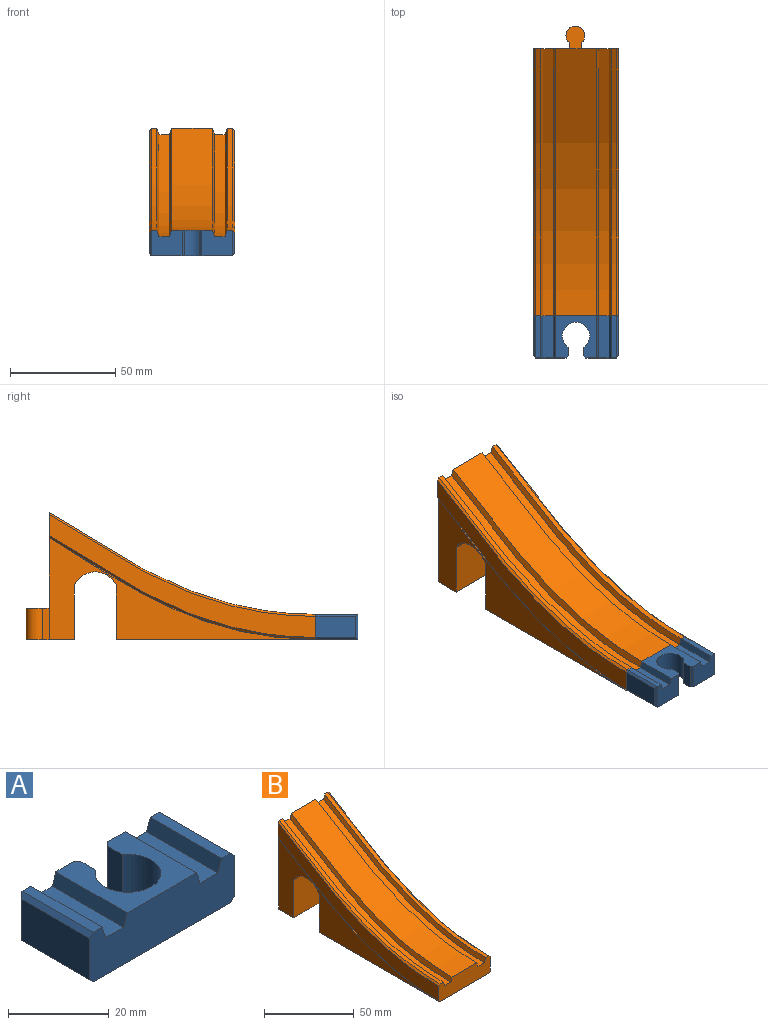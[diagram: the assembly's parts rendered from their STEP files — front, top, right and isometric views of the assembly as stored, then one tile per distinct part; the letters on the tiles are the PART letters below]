
ASSEMBLY  parts=2 mates=1
PART A: 26 faces, bbox 40.5x20x12 mm
  f0: plane 38.5x20mm, normal (0,0,-1), area 603.4mm2, adj f2,f13,f14,f15,f16,f17,f18,f21
  f1: plane 20x19.5mm, normal (0,0,1), area 223.4mm2, adj f2,f7,f8,f13,f14,f15,f16,f17
  f2: plane 14.51x12mm, normal (0,1,0), area 156.1mm2, adj f0,f1,f8,f9,f10,f11,f20,f21
  f3: plane 19x10mm, normal (1,0,0), area 190mm2, adj f14,f23,f24,f25
  f4: plane 20x2.5mm, normal (0,0,1), area 50mm2, adj f5,f13,f14,f24
  f5: plane 20x3mm, normal (-0.95,0,0.32), area 63.2mm2, adj f4,f6,f13,f14
  f6: plane 20x5mm, normal (0,0,1), area 100mm2, adj f5,f7,f13,f14
  f7: plane 20x3mm, normal (0.95,0,0.32), area 63.2mm2, adj f1,f6,f13,f14
  f8: plane 20x3mm, normal (-0.95,0,0.32), area 63.2mm2, adj f1,f2,f9,f14
  f9: plane 20x5mm, normal (0,0,1), area 100mm2, adj f2,f8,f10,f14
  f10: plane 20x3mm, normal (0.95,0,0.32), area 63.2mm2, adj f2,f9,f11,f14
  f11: plane 20x2.5mm, normal (0,0,1), area 50mm2, adj f2,f10,f14,f19
  f12: plane 19x10mm, normal (-1,0,0), area 190mm2, adj f14,f18,f19,f20
  f13: plane 14.49x12mm, normal (0,1,0), area 155.9mm2, adj f0,f1,f4,f5,f6,f7,f22,f25
  f14: plane 40.5x12mm, normal (0,-1,0), area 448mm2, adj f0,f1,f3,f4,f5,f6,f7,f8
  f15: cylinder r=6.5mm len=13mm, axis (0,0,1), area 394.2mm2, adj f0,f1,f16,f17
  f16: plane 12x4.19mm, normal (1,0,0), area 50.3mm2, adj f0,f1,f15,f21
  f17: plane 12x4.19mm, normal (-1,0,0), area 50.3mm2, adj f0,f1,f15,f22
  f18: plane 20x1mm, normal (-0.71,0,-0.71), area 27.6mm2, adj f0,f12,f14,f20
  f19: plane 20x1mm, normal (-0.71,0,0.71), area 27.6mm2, adj f11,f12,f14,f20
  f20: plane 12x1mm, normal (-0.71,0.71,0), area 15.6mm2, adj f2,f12,f18,f19
  f21: plane 12x1mm, normal (0.71,0.71,0), area 17mm2, adj f0,f1,f2,f16
  f22: plane 12x1mm, normal (-0.71,0.71,0), area 17mm2, adj f0,f1,f13,f17
  f23: plane 20x1mm, normal (0.71,0,-0.71), area 27.6mm2, adj f0,f3,f14,f25
  f24: plane 20x1mm, normal (0.71,0,0.71), area 27.6mm2, adj f3,f4,f14,f25
  f25: plane 12x1mm, normal (0.71,0.71,0), area 15.6mm2, adj f3,f13,f23,f24
PART B: 29 faces, bbox 40.5x235x97 mm
  f0: plane 60.46x40.5mm, normal (0,1,0), area 2251.5mm2, adj f1,f7,f8,f9,f10,f11,f12,f13
  f1: plane 39x22.96mm, normal (0,0,-1), area 544.8mm2, adj f0,f2,f23,f24,f25,f26,f27
  f2: plane 39x26mm, normal (0,-1,0), area 1014mm2, adj f1,f3,f23,f24
  f3: cylinder r=11.18mm len=39mm, axis (1,0,0), area 965.2mm2, adj f2,f4,f23,f24
  f4: plane 39x26mm, normal (0,1,0), area 1014mm2, adj f3,f6,f23,f24
  f5: plane 40.5x12mm, normal (0,-1,0), area 448mm2, adj f6,f8,f9,f10,f11,f12,f13,f14
  f6: plane 95x39mm, normal (0,0,-1), area 3705mm2, adj f4,f5,f7,f23,f24
  f7: extruded ~127x48.46mm, area 69.1mm2, adj f0,f6,f8,f24
  f8: bspline ~235x86mm, area 187.7mm2, adj f0,f5,f7,f22
  f9: bspline ~235x86mm, area 187.7mm2, adj f0,f5,f10,f22
  f10: bspline ~235x85mm, area 345.4mm2, adj f0,f5,f9,f11
  f11: bspline ~235x88mm, area 405.4mm2, adj f0,f5,f10,f12
  f12: bspline ~235x85mm, area 690.8mm2, adj f0,f5,f11,f13
  f13: bspline ~235x88mm, area 405.4mm2, adj f0,f5,f12,f14
  f14: bspline ~235x85mm, area 2694mm2, adj f0,f5,f13,f15
  f15: bspline ~235x88mm, area 405.4mm2, adj f0,f5,f14,f16
  f16: bspline ~235x85mm, area 690.8mm2, adj f0,f5,f15,f17
  f17: bspline ~235x88mm, area 405.4mm2, adj f0,f5,f16,f18
  f18: bspline ~235x85mm, area 345.4mm2, adj f0,f5,f17,f19
  f19: bspline ~235x86mm, area 187.7mm2, adj f0,f5,f18,f21
  f20: bspline ~235x86mm, area 187.7mm2, adj f0,f5,f21,f23
  f21: plane 130.27x61.73mm, normal (1,0,0), area 1270mm2, adj f0,f5,f19,f20
  f22: plane 130.27x61.73mm, normal (-1,0,0), area 1270mm2, adj f0,f5,f8,f9
  f23: plane 130.27x51.73mm, normal (1,0,0), area 1523.8mm2, adj f0,f1,f2,f3,f4,f6,f20
  f24: plane 130.27x51.73mm, normal (-1,0,0), area 1523.8mm2, adj f0,f1,f2,f3,f4,f6,f7
  f25: cylinder r=4.5mm len=15mm, axis (0,0,-1), area 330.6mm2, adj f1,f26,f27,f28
  f26: plane 15x3mm, normal (1,0,0), area 45mm2, adj f0,f1,f25,f28
  f27: plane 15x3mm, normal (-1,0,0), area 45mm2, adj f0,f1,f25,f28
  f28: plane 10.96x9mm, normal (0,0,1), area 76.8mm2, adj f0,f25,f26,f27
PLACE A rot(axis=(0,0,1),180deg) t=(-86.55,-153.74,-82.42)mm
PLACE B t=(-88.39,148,-3.61)mm
MATE fastened A.f14 <-> B.f5  axis (0,1,0) through (-86.55,-153.74,-76.79)mm
